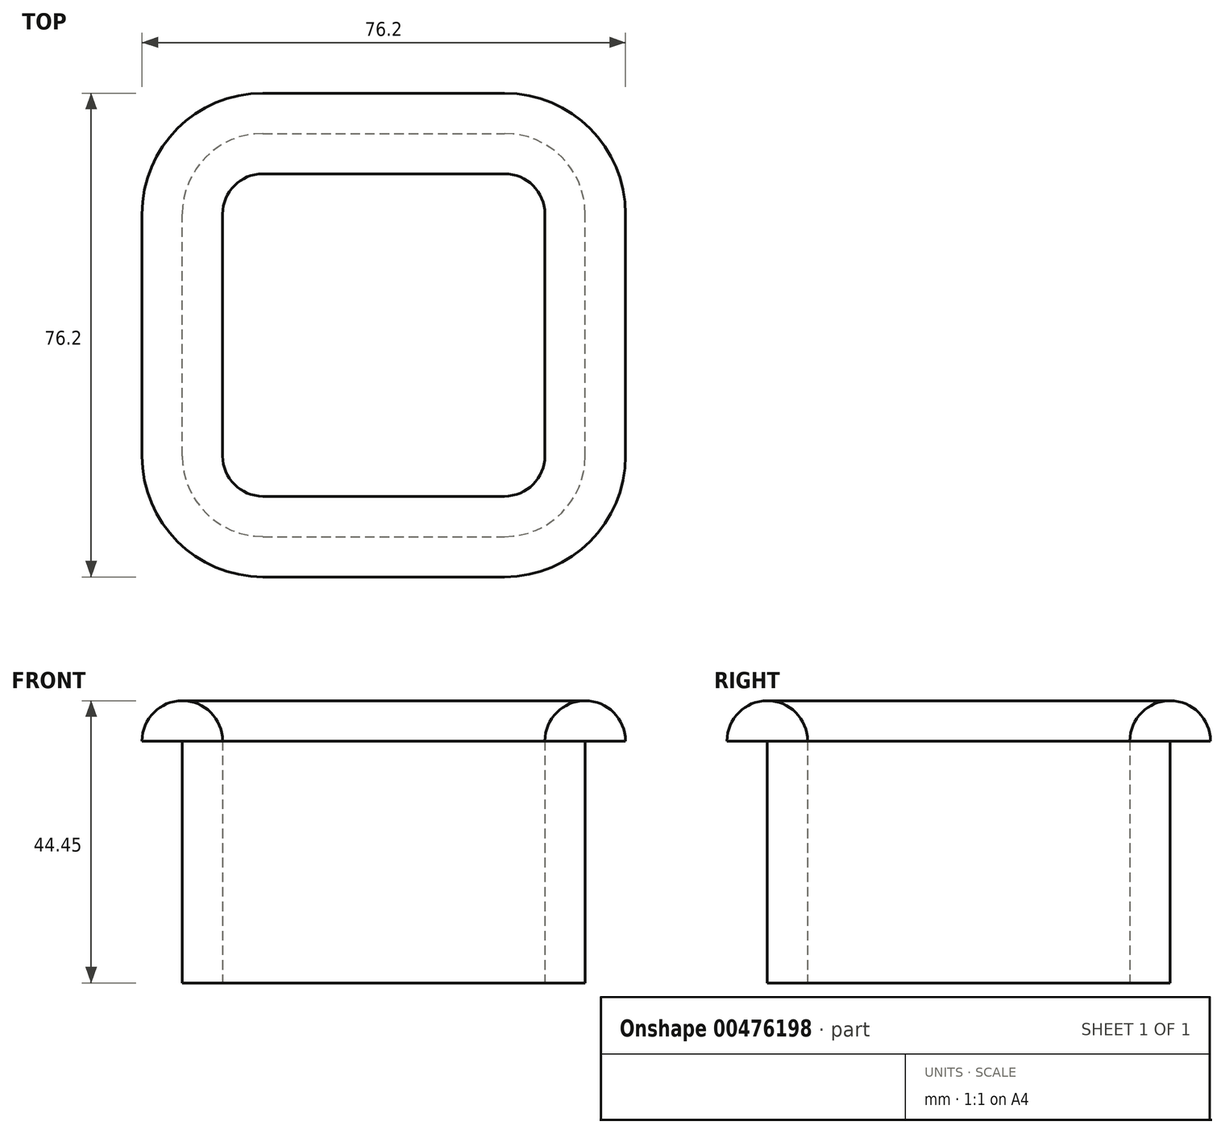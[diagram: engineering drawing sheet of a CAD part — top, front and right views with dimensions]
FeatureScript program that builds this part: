
annotation { "Feature Type Name" : "Feature", "Feature Type Description" : "" }
export const myFeature = defineFeature(function(context is Context, id is Id, definition is map)
    precondition{}
    {
        {
            var Q0;
            Q0=qCreatedBy(makeId("Top.planeOp"),FACE);
            var sketch = newSketch(context, id + "F0", { "sketchPlane" : qUnion([Q0])});
            skLineSegment(sketch, "E0.bottom", {"start": v(-19.05, -25.4) * mm, "end": v(19.05, -25.4) * mm});
            skLineSegment(sketch, "E0.top", {"start": v(-19.05, 25.4) * mm, "end": v(19.05, 25.4) * mm});
            skLineSegment(sketch, "E0.left", {"start": v(-25.4, -19.05) * mm, "end": v(-25.4, 19.05) * mm});
            skLineSegment(sketch, "E0.right", {"start": v(25.4, -19.05) * mm, "end": v(25.4, 19.05) * mm});
            skPoint(sketch, "E1.visualSharp", {"position": v(25.4, 25.4) * mm});
            skArc(sketch, "E1.filletArc", {"start": v(25.4, 19.05) * mm, "mid": v(23.54, 23.54) * mm, "end": v(19.05, 25.4) * mm});
            skPoint(sketch, "E2.visualSharp", {"position": v(-25.4, 25.4) * mm});
            skArc(sketch, "E2.filletArc", {"start": v(-19.05, 25.4) * mm, "mid": v(-23.54, 23.54) * mm, "end": v(-25.4, 19.05) * mm});
            skPoint(sketch, "E3.visualSharp", {"position": v(25.4, -25.4) * mm});
            skArc(sketch, "E3.filletArc", {"start": v(19.05, -25.4) * mm, "mid": v(23.54, -23.54) * mm, "end": v(25.4, -19.05) * mm});
            skPoint(sketch, "E4.visualSharp", {"position": v(-17.67, -28.86) * mm});
            skArc(sketch, "E4.filletArc", {"start": v(-25.4, -19.05) * mm, "mid": v(-23.54, -23.54) * mm, "end": v(-19.05, -25.4) * mm});
            skArc(sketch, "E5.0", {"start": v(-31.75, -19.05) * mm, "mid": v(-28.03, -28.03) * mm, "end": v(-19.05, -31.75) * mm});
            skLineSegment(sketch, "E5.1", {"start": v(-19.05, -31.75) * mm, "end": v(19.05, -31.75) * mm});
            skLineSegment(sketch, "E5.2", {"start": v(-31.75, -19.05) * mm, "end": v(-31.75, 19.05) * mm});
            skArc(sketch, "E5.3", {"start": v(19.05, -31.75) * mm, "mid": v(28.03, -28.03) * mm, "end": v(31.75, -19.05) * mm});
            skArc(sketch, "E5.4", {"start": v(-19.05, 31.75) * mm, "mid": v(-28.03, 28.03) * mm, "end": v(-31.75, 19.05) * mm});
            skLineSegment(sketch, "E5.5", {"start": v(-19.05, 31.75) * mm, "end": v(19.05, 31.75) * mm});
            skArc(sketch, "E5.6", {"start": v(31.75, 19.05) * mm, "mid": v(28.03, 28.03) * mm, "end": v(19.05, 31.75) * mm});
            skLineSegment(sketch, "E5.7", {"start": v(31.75, -19.05) * mm, "end": v(31.75, 19.05) * mm});
            skArc(sketch, "E6.0", {"start": v(19.05, -38.1) * mm, "mid": v(32.52, -32.52) * mm, "end": v(38.1, -19.05) * mm});
            skLineSegment(sketch, "E6.1", {"start": v(-19.05, -38.1) * mm, "end": v(19.05, -38.1) * mm});
            skLineSegment(sketch, "E6.2", {"start": v(38.1, -19.05) * mm, "end": v(38.1, 19.05) * mm});
            skArc(sketch, "E6.3", {"start": v(-38.1, -19.05) * mm, "mid": v(-32.52, -32.52) * mm, "end": v(-19.05, -38.1) * mm});
            skArc(sketch, "E6.4", {"start": v(38.1, 19.05) * mm, "mid": v(32.52, 32.52) * mm, "end": v(19.05, 38.1) * mm});
            skLineSegment(sketch, "E6.5", {"start": v(-19.05, 38.1) * mm, "end": v(19.05, 38.1) * mm});
            skArc(sketch, "E6.6", {"start": v(-19.05, 38.1) * mm, "mid": v(-32.52, 32.52) * mm, "end": v(-38.1, 19.05) * mm});
            skLineSegment(sketch, "E6.7", {"start": v(-38.1, -19.05) * mm, "end": v(-38.1, 19.05) * mm});
            skPoint(sketch, "E7", {"position": v(0, 0) * mm});
            skPoint(sketch, "E7.positionSnap0", {"position": v(0, 25.4) * mm});
            skPoint(sketch, "E7.positionSnap1", {"position": v(-25.4, 0) * mm});
            skSolve(sketch);
        }
        {
            var Q0;
            Q0=makeQuery(id+"F0.imprint","IMPRINT",FACE,{"disambiguationData":[TD([[makeQuery(id+"F0.imprint","IMPRINT",EDGE,{"derivedFrom":sQuery(id+"F0.wireOp",EDGE,"E0.bottom")}),-1.0]])]});
            var Q1;
            Q1=makeQuery(id+"F0.imprint","IMPRINT",FACE,{"disambiguationData":[TD([[makeQuery(id+"F0.imprint","IMPRINT",EDGE,{"derivedFrom":sQuery(id+"F0.wireOp",EDGE,"E5.0")}),-1.0]])]});
            extrude(context, id + "F1", {"entities" : qUnion([Q0, Q1]), "depth" : 6.35 * mm});
        }
        {
            var Q0;
            Q0=makeQuery(id+"F0.imprint","IMPRINT",FACE,{"disambiguationData":[TD([[makeQuery(id+"F0.imprint","IMPRINT",EDGE,{"derivedFrom":sQuery(id+"F0.wireOp",EDGE,"E0.bottom")}),-1.0]])]});
            extrude(context, id + "F2", {"entities" : qUnion([Q0]), "operationType" : NewBodyOperationType.ADD, "oppositeDirection" : true, "depth" : 38.1 * mm});
        }
        {
            var Q0;
            Q0=makeQuery(id+"F1.opExtrude","CAP_FACE",FACE,{"disambiguationData":[OSD([sQuery(id+"F0.wireOp",EDGE,"E0.bottom"),sQuery(id+"F0.wireOp",EDGE,"E0.top"),sQuery(id+"F0.wireOp",EDGE,"E0.left"),sQuery(id+"F0.wireOp",EDGE,"E0.right"),sQuery(id+"F0.wireOp",EDGE,"E1.filletArc"),sQuery(id+"F0.wireOp",EDGE,"E2.filletArc"),sQuery(id+"F0.wireOp",EDGE,"E3.filletArc"),sQuery(id+"F0.wireOp",EDGE,"E4.filletArc"),sQuery(id+"F0.wireOp",EDGE,"E6.0"),sQuery(id+"F0.wireOp",EDGE,"E6.1"),sQuery(id+"F0.wireOp",EDGE,"E6.2"),sQuery(id+"F0.wireOp",EDGE,"E6.3"),sQuery(id+"F0.wireOp",EDGE,"E6.4"),sQuery(id+"F0.wireOp",EDGE,"E6.5"),sQuery(id+"F0.wireOp",EDGE,"E6.6"),sQuery(id+"F0.wireOp",EDGE,"E6.7")])],"isStart":false});
            fillet(context, id + "F3", {"entities" : qUnion([Q0]), "radius" : 6.35 * mm, "tangentPropagation" : true, "allowEdgeOverflow" : false});
        }
    });
